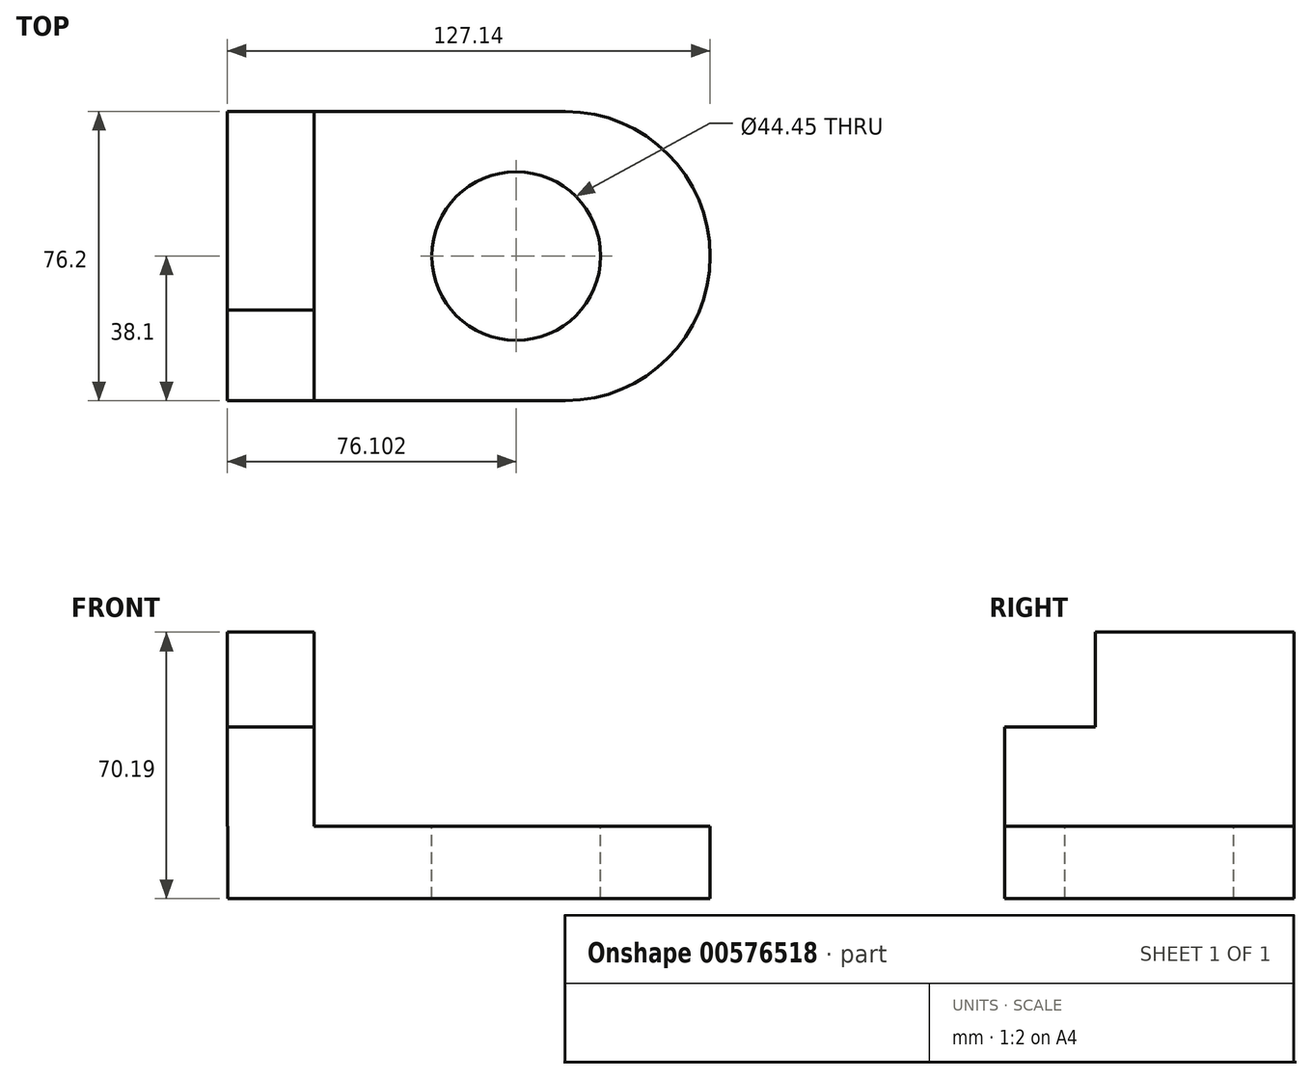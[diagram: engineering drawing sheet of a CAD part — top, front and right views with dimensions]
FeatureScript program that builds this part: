
annotation { "Feature Type Name" : "Feature", "Feature Type Description" : "" }
export const myFeature = defineFeature(function(context is Context, id is Id, definition is map)
    precondition{}
    {
        {
            var Q0;
            Q0=qCreatedBy(makeId("Top.planeOp"),FACE);
            var sketch = newSketch(context, id + "F0", { "sketchPlane" : qUnion([Q0])});
            skLineSegment(sketch, "E0.bottom", {"start": v(-63.5, 38.1) * mm, "end": v(25.4, 38.1) * mm});
            skLineSegment(sketch, "E0.top", {"start": v(-63.5, -38.1) * mm, "end": v(25.4, -38.1) * mm});
            skLineSegment(sketch, "E0.left", {"start": v(-63.5, 38.1) * mm, "end": v(-63.5, -38.1) * mm});
            skLineSegment(sketch, "E0.right", {"start": v(63.5, 0) * mm, "end": v(63.5, 0) * mm});
            skPoint(sketch, "E0.middle", {"position": v(0, 0) * mm});
            skPoint(sketch, "E1.visualSharp", {"position": v(63.5, 38.1) * mm});
            skArc(sketch, "E1.filletArc", {"start": v(63.5, 0) * mm, "mid": v(52.34, 26.94) * mm, "end": v(25.4, 38.1) * mm});
            skPoint(sketch, "E2.visualSharp", {"position": v(63.5, -38.1) * mm});
            skArc(sketch, "E2.filletArc", {"start": v(25.4, -38.1) * mm, "mid": v(52.34, -26.94) * mm, "end": v(63.5, 0) * mm});
            skSolve(sketch);
        }
        {
            var Q0;
            Q0=makeQuery(id+"F0.imprint","IMPRINT",FACE,{"disambiguationData":[TD([[makeQuery(id+"F0.imprint","IMPRINT",EDGE,{"derivedFrom":sQuery(id+"F0.wireOp",EDGE,"E0.bottom")}),-1.0]])]});
            extrude(context, id + "F1", {"entities" : qUnion([Q0]), "oppositeDirection" : true, "depth" : 19.05 * mm, "offsetDistance" : 25.4 * mm});
        }
        {
            var Q0;
            Q0=qCreatedBy(makeId("Front.planeOp"),FACE);
            var sketch = newSketch(context, id + "F2", { "sketchPlane" : qUnion([Q0])});
            skLineSegment(sketch, "E3.bottom", {"start": v(-63.64, 0) * mm, "end": v(-40.83, 0) * mm});
            skLineSegment(sketch, "E3.top", {"start": v(-63.64, 51.14) * mm, "end": v(-40.83, 51.14) * mm});
            skLineSegment(sketch, "E3.left", {"start": v(-63.64, 0) * mm, "end": v(-63.64, 51.14) * mm});
            skLineSegment(sketch, "E3.right", {"start": v(-40.83, 0) * mm, "end": v(-40.83, 51.14) * mm});
            skSolve(sketch);
        }
        {
            var Q0;
            Q0=makeQuery(id+"F2.imprint","IMPRINT",FACE,{"disambiguationData":[TD([[makeQuery(id+"F2.imprint","IMPRINT",EDGE,{"derivedFrom":sQuery(id+"F2.wireOp",EDGE,"E3.bottom")}),1.0]])]});
            extrude(context, id + "F3", {"entities" : qUnion([Q0]), "operationType" : NewBodyOperationType.ADD, "endBound" : BoundingType.SYMMETRIC, "depth" : 76.2 * mm, "offsetDistance" : 25.4 * mm});
        }
        {
            var Q0;
            Q0=makeQuery(id+"F3.opExtrude","SWEPT_FACE",FACE,{"disambiguationData":[OSD([sQuery(id+"F2.wireOp",EDGE,"E3.left")])]});
            var sketch = newSketch(context, id + "F4", { "sketchPlane" : qUnion([Q0])});
            skLineSegment(sketch, "E4.bottom", {"start": v(38.1, 51.14) * mm, "end": v(14.18, 51.14) * mm});
            skLineSegment(sketch, "E4.top", {"start": v(38.1, 26.21) * mm, "end": v(14.18, 26.21) * mm});
            skLineSegment(sketch, "E4.left", {"start": v(38.1, 51.14) * mm, "end": v(38.1, 26.21) * mm});
            skLineSegment(sketch, "E4.right", {"start": v(14.18, 51.14) * mm, "end": v(14.18, 26.21) * mm});
            skSolve(sketch);
        }
        {
            var Q0;
            Q0=makeQuery(id+"F4.imprint","IMPRINT",FACE,{"disambiguationData":[TD([[makeQuery(id+"F4.imprint","IMPRINT",EDGE,{"derivedFrom":sQuery(id+"F4.wireOp",EDGE,"E4.bottom")}),1.0]])]});
            extrude(context, id + "F5", {"entities" : qUnion([Q0]), "operationType" : NewBodyOperationType.REMOVE, "oppositeDirection" : true, "depth" : 25.4 * mm, "offsetDistance" : 25.4 * mm});
        }
        {
            var Q0;
            Q0=makeQuery(id+"F1.opExtrude","CAP_FACE",FACE,{"disambiguationData":[OSD([sQuery(id+"F0.wireOp",EDGE,"E0.bottom"),sQuery(id+"F0.wireOp",EDGE,"E0.top"),sQuery(id+"F0.wireOp",EDGE,"E0.left"),sQuery(id+"F0.wireOp",EDGE,"E0.right")])],"isStart":true});
            var sketch = newSketch(context, id + "F6", { "sketchPlane" : qUnion([Q0])});
            skCircle(sketch, "E5", {"center": v(12.46, 0) * mm, "radius": 23.05 * mm});
            skSolve(sketch);
        }
        {
            var Q0;
            Q0=sQuery(id+"F6.wireOp",VERTEX,"E5.center");
            var Q1;
            Q1=makeQuery(id+"F1.opExtrude","SWEPT_BODY",BODY,{"disambiguationData":[OSD([sQuery(id+"F0.wireOp",EDGE,"E0.bottom"),sQuery(id+"F0.wireOp",EDGE,"E0.top"),sQuery(id+"F0.wireOp",EDGE,"E0.left"),sQuery(id+"F0.wireOp",EDGE,"E0.right")])]});
            hole(context, id + "F7", {"style" : HoleStyle.SIMPLE, "endStyle" : HoleEndStyle.THROUGH, "holeDiameter" : 44.45 * mm, "isTappedThrough" : true, "tappedDepth" : 12.7 * mm, "tapClearance" : 3, "locations" : qUnion([Q0]), "scope" : qUnion([Q1])});
        }
    });
